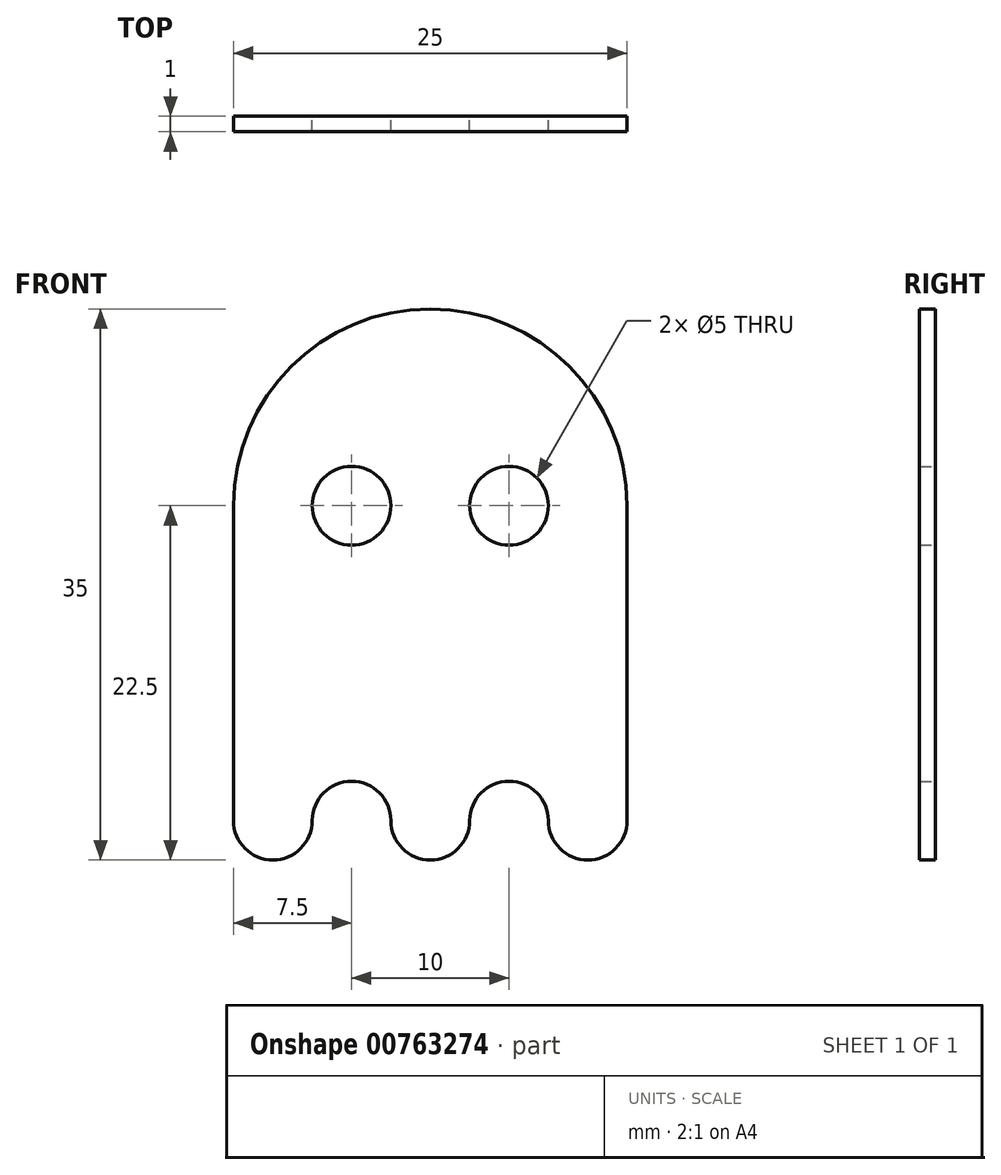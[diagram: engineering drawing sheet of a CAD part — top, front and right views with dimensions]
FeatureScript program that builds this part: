
annotation { "Feature Type Name" : "Feature", "Feature Type Description" : "" }
export const myFeature = defineFeature(function(context is Context, id is Id, definition is map)
    precondition{}
    {
        {
            var Q0;
            Q0=qCreatedBy(makeId("Front.planeOp"),FACE);
            var sketch = newSketch(context, id + "F0", { "sketchPlane" : qUnion([Q0])});
            skArc(sketch, "E0", {"start": v(-12.5, 0) * mm, "mid": v(0, 12.5) * mm, "end": v(12.5, 0) * mm});
            skLineSegment(sketch, "E1", {"start": v(12.5, 0) * mm, "end": v(12.5, -20) * mm});
            skArc(sketch, "E2", {"start": v(12.5, -20) * mm, "mid": v(10, -22.5) * mm, "end": v(7.5, -20) * mm});
            skArc(sketch, "E3", {"start": v(7.5, -20) * mm, "mid": v(5, -17.5) * mm, "end": v(2.5, -20) * mm});
            skArc(sketch, "E4", {"start": v(2.5, -20) * mm, "mid": v(1.77, -21.77) * mm, "end": v(0, -22.5) * mm});
            skLineSegment(sketch, "E5", {"start": v(0, 0) * mm, "end": v(0, -9) * mm, "construction": true});
            skArc(sketch, "E6.MirrorCS", {"start": v(-12.5, -20) * mm, "mid": v(-10, -22.5) * mm, "end": v(-7.5, -20) * mm});
            skArc(sketch, "E7.MirrorCS", {"start": v(-7.5, -20) * mm, "mid": v(-5, -17.5) * mm, "end": v(-2.5, -20) * mm});
            skArc(sketch, "E8.MirrorCS", {"start": v(-2.5, -20) * mm, "mid": v(-1.77, -21.77) * mm, "end": v(0, -22.5) * mm});
            skLineSegment(sketch, "E9.MirrorCS", {"start": v(-12.5, 0) * mm, "end": v(-12.5, -20) * mm});
            skCircle(sketch, "E10", {"center": v(-5, 0) * mm, "radius": 2.5 * mm});
            skCircle(sketch, "E11.MirrorC", {"center": v(5, 0) * mm, "radius": 2.5 * mm});
            skSolve(sketch);
        }
        {
            var Q0;
            Q0 = qSketchRegion(id + "F0", true);
            extrude(context, id + "F1", {"entities" : qUnion([Q0]), "depth" : 1 * mm, "offsetDistance" : 25 * mm});
        }
    });
